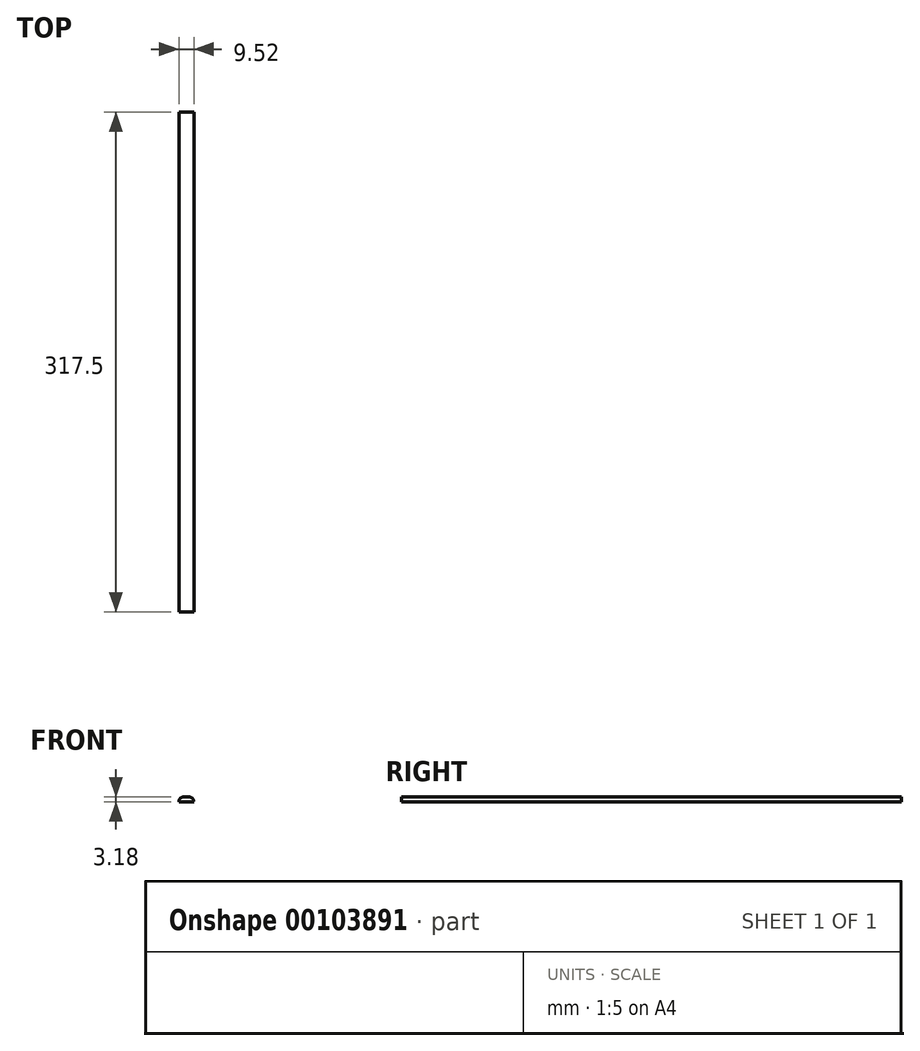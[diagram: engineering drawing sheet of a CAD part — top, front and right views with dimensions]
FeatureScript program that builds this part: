
annotation { "Feature Type Name" : "Feature", "Feature Type Description" : "" }
export const myFeature = defineFeature(function(context is Context, id is Id, definition is map)
    precondition{}
    {
        {
            var Q0;
            Q0=qCreatedBy(makeId("Front.planeOp"),FACE);
            var sketch = newSketch(context, id + "F0", { "sketchPlane" : qUnion([Q0])});
            skLineSegment(sketch, "E0.bottom", {"start": v(4.76, 1.59) * mm, "end": v(-4.76, 1.59) * mm});
            skLineSegment(sketch, "E0.top", {"start": v(4.76, -1.59) * mm, "end": v(-4.76, -1.59) * mm});
            skLineSegment(sketch, "E0.left", {"start": v(4.76, 1.59) * mm, "end": v(4.76, -1.59) * mm});
            skLineSegment(sketch, "E0.right", {"start": v(-4.76, 1.59) * mm, "end": v(-4.76, -1.59) * mm});
            skPoint(sketch, "E0.middle", {"position": v(0, 0) * mm});
            skSolve(sketch);
        }
        {
            var Q0;
            Q0=makeQuery(id+"F0.imprint","IMPRINT",FACE,{"disambiguationData":[TD([[makeQuery(id+"F0.imprint","IMPRINT",EDGE,{"derivedFrom":sQuery(id+"F0.wireOp",EDGE,"E0.bottom")}),1.0]])]});
            extrude(context, id + "F1", {"entities" : qUnion([Q0]), "depth" : 317.5 * mm});
        }
        {
            var Q0;
            Q0=makeQuery(id+"F1.opExtrude","SWEPT_EDGE",EDGE,{"disambiguationData":[OSD([sQuery(id+"F0.wireOp",EDGE,"E0.bottom"),sQuery(id+"F0.wireOp",EDGE,"E0.right")])]});
            var Q1;
            Q1=makeQuery(id+"F1.opExtrude","SWEPT_EDGE",EDGE,{"disambiguationData":[OSD([sQuery(id+"F0.wireOp",EDGE,"E0.bottom"),sQuery(id+"F0.wireOp",EDGE,"E0.left")])]});
            fillet(context, id + "F2", {"entities" : qUnion([Q0, Q1]), "radius" : 3.17 * mm, "tangentPropagation" : true, "allowEdgeOverflow" : false});
        }
    });
